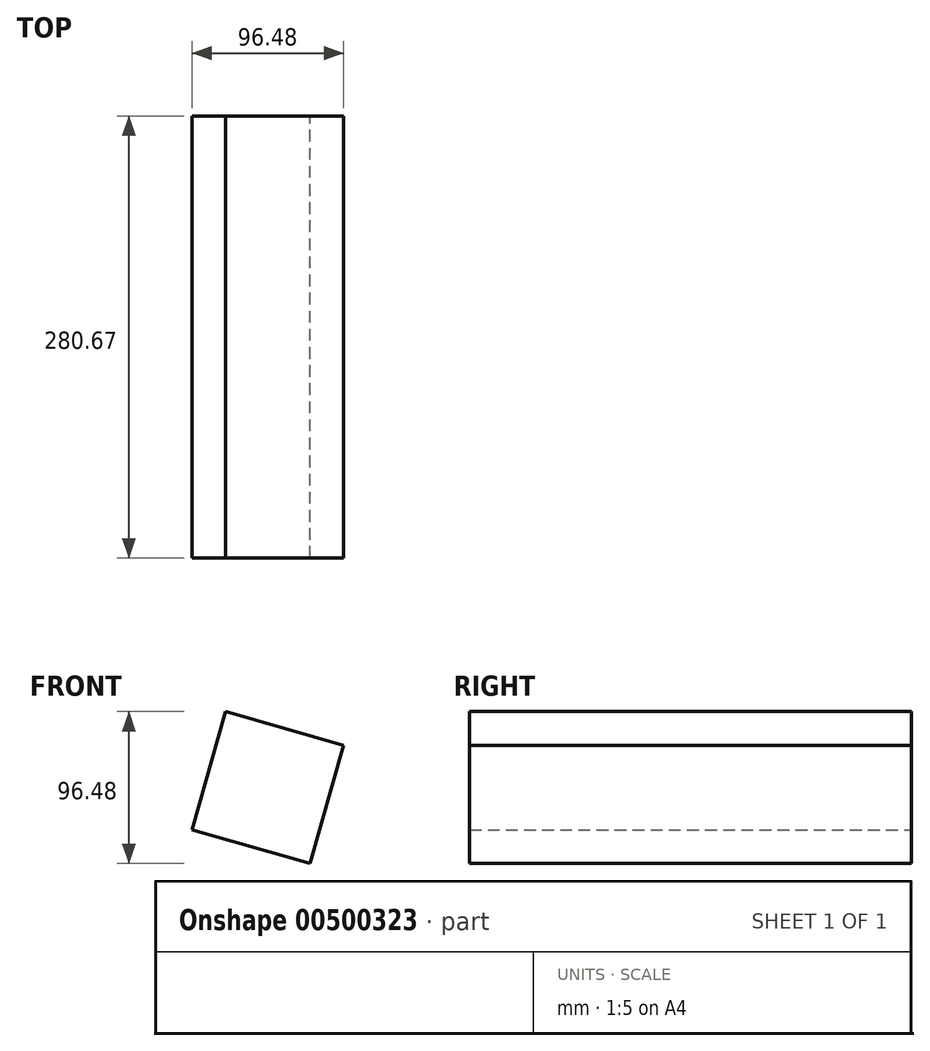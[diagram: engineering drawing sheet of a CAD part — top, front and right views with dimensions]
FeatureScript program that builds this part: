
annotation { "Feature Type Name" : "Feature", "Feature Type Description" : "" }
export const myFeature = defineFeature(function(context is Context, id is Id, definition is map)
    precondition{}
    {
        {
            var Q0;
            Q0=qCreatedBy(makeId("Front.planeOp"),FACE);
            var sketch = newSketch(context, id + "F0", { "sketchPlane" : qUnion([Q0])});
            skCircle(sketch, "E0.cCircle", {"center": v(0, 0) * mm, "radius": 55.2 * mm, "construction": true});
            skLineSegment(sketch, "E0.0", {"start": v(-26.82, 48.24) * mm, "end": v(48.24, 26.82) * mm});
            skLineSegment(sketch, "E0.1", {"start": v(48.24, 26.82) * mm, "end": v(26.82, -48.24) * mm});
            skLineSegment(sketch, "E0.2", {"start": v(26.82, -48.24) * mm, "end": v(-48.24, -26.82) * mm});
            skLineSegment(sketch, "E0.3", {"start": v(-48.24, -26.82) * mm, "end": v(-26.82, 48.24) * mm});
            skSolve(sketch);
        }
        {
            var Q0;
            Q0 = qSketchRegion(id + "F0", true);
            extrude(context, id + "F1", {"entities" : qUnion([Q0]), "depth" : 280.67 * mm});
        }
    });
